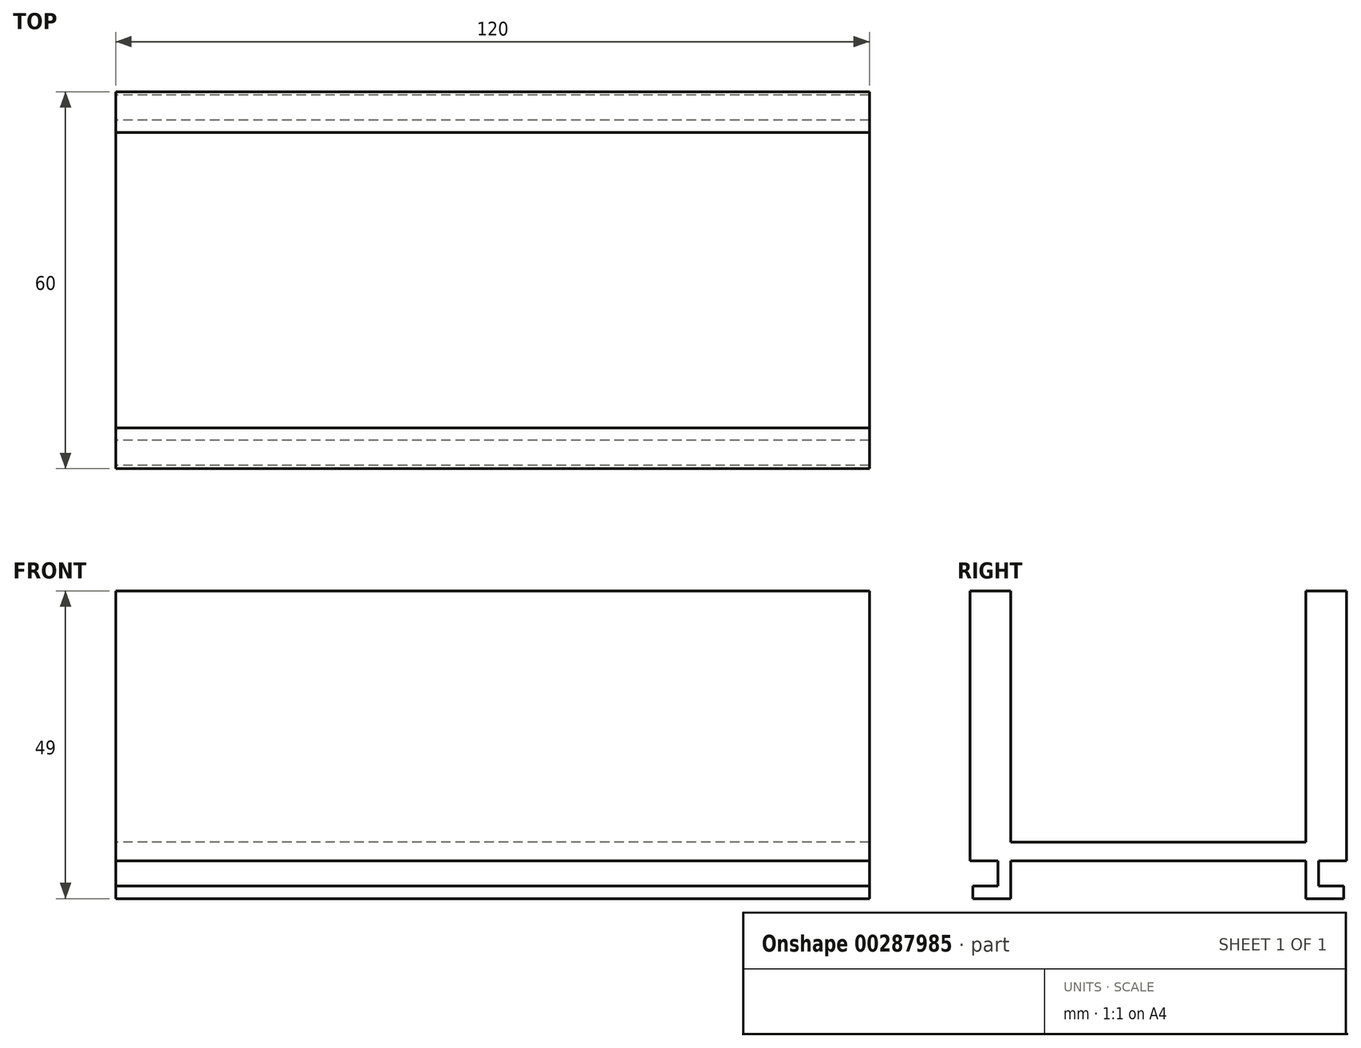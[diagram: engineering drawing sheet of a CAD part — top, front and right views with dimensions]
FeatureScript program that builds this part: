
annotation { "Feature Type Name" : "Feature", "Feature Type Description" : "" }
export const myFeature = defineFeature(function(context is Context, id is Id, definition is map)
    precondition{}
    {
        {
            var Q0;
            Q0=qCreatedBy(makeId("Right.planeOp"),FACE);
            var sketch = newSketch(context, id + "F0", { "sketchPlane" : qUnion([Q0])});
            skLineSegment(sketch, "E0.top", {"start": v(-30, -3) * mm, "end": v(30, -3) * mm});
            skLineSegment(sketch, "E0.left", {"start": v(-30, 0) * mm, "end": v(-30, -3) * mm});
            skLineSegment(sketch, "E0.right", {"start": v(30, 0) * mm, "end": v(30, -3) * mm});
            skLineSegment(sketch, "E1", {"start": v(25.5, -3) * mm, "end": v(-25.5, -3) * mm});
            skLineSegment(sketch, "E2", {"start": v(-25.5, -3) * mm, "end": v(-23.5, -3) * mm});
            skLineSegment(sketch, "E3", {"start": v(-23.5, -3) * mm, "end": v(23.5, -3) * mm});
            skLineSegment(sketch, "E4", {"start": v(23.5, -3) * mm, "end": v(25.5, -3) * mm});
            skLineSegment(sketch, "E5.top", {"start": v(-25.5, -7) * mm, "end": v(-23.5, -7) * mm});
            skLineSegment(sketch, "E5.left", {"start": v(-25.5, -3) * mm, "end": v(-25.5, -7) * mm});
            skLineSegment(sketch, "E5.right", {"start": v(-23.5, -3) * mm, "end": v(-23.5, -7) * mm});
            skLineSegment(sketch, "E6.bottom", {"start": v(-23.5, -7) * mm, "end": v(-29.5, -7) * mm});
            skLineSegment(sketch, "E6.top", {"start": v(-23.5, -9) * mm, "end": v(-29.5, -9) * mm});
            skLineSegment(sketch, "E6.left", {"start": v(-23.5, -7) * mm, "end": v(-23.5, -9) * mm});
            skLineSegment(sketch, "E6.right", {"start": v(-29.5, -7) * mm, "end": v(-29.5, -9) * mm});
            skLineSegment(sketch, "E7.MirrorCS", {"start": v(25.5, -3) * mm, "end": v(23.5, -3) * mm});
            skLineSegment(sketch, "E8.MirrorCS", {"start": v(23.5, -7) * mm, "end": v(23.5, -9) * mm});
            skLineSegment(sketch, "E9.MirrorCS", {"start": v(25.5, -7) * mm, "end": v(23.5, -7) * mm});
            skLineSegment(sketch, "E10.MirrorCS", {"start": v(23.5, -3) * mm, "end": v(23.5, -7) * mm});
            skLineSegment(sketch, "E11.MirrorCS", {"start": v(29.5, -7) * mm, "end": v(29.5, -9) * mm});
            skLineSegment(sketch, "E12.MirrorCS", {"start": v(23.5, -9) * mm, "end": v(29.5, -9) * mm});
            skLineSegment(sketch, "E13.MirrorCS", {"start": v(25.5, -3) * mm, "end": v(25.5, -7) * mm});
            skLineSegment(sketch, "E14.MirrorCS", {"start": v(23.5, -7) * mm, "end": v(29.5, -7) * mm});
            skLineSegment(sketch, "E15.bottom", {"start": v(-30, 0) * mm, "end": v(30, 0) * mm});
            skLineSegment(sketch, "E16.bottom", {"start": v(-30, 0) * mm, "end": v(-23.5, 0) * mm});
            skLineSegment(sketch, "E16.top", {"start": v(-30, 40) * mm, "end": v(-23.5, 40) * mm});
            skLineSegment(sketch, "E16.left", {"start": v(-30, 0) * mm, "end": v(-30, 40) * mm});
            skLineSegment(sketch, "E16.right", {"start": v(-23.5, 0) * mm, "end": v(-23.5, 40) * mm});
            skLineSegment(sketch, "E17.bottom", {"start": v(30, 0) * mm, "end": v(23.5, 0) * mm});
            skLineSegment(sketch, "E17.top", {"start": v(30, 40) * mm, "end": v(23.5, 40) * mm});
            skLineSegment(sketch, "E17.left", {"start": v(30, 0) * mm, "end": v(30, 40) * mm});
            skLineSegment(sketch, "E17.right", {"start": v(23.5, 0) * mm, "end": v(23.5, 40) * mm});
            skSolve(sketch);
        }
        {
            var Q0;
            Q0 = qSketchRegion(id + "F0", true);
            extrude(context, id + "F1", {"entities" : qUnion([Q0]), "offsetDistance" : 25 * mm, "depth" : 60 * mm, "hasSecondDirection" : true, "secondDirectionOppositeDirection" : true, "secondDirectionDepth" : 60 * mm});
        }
    });
